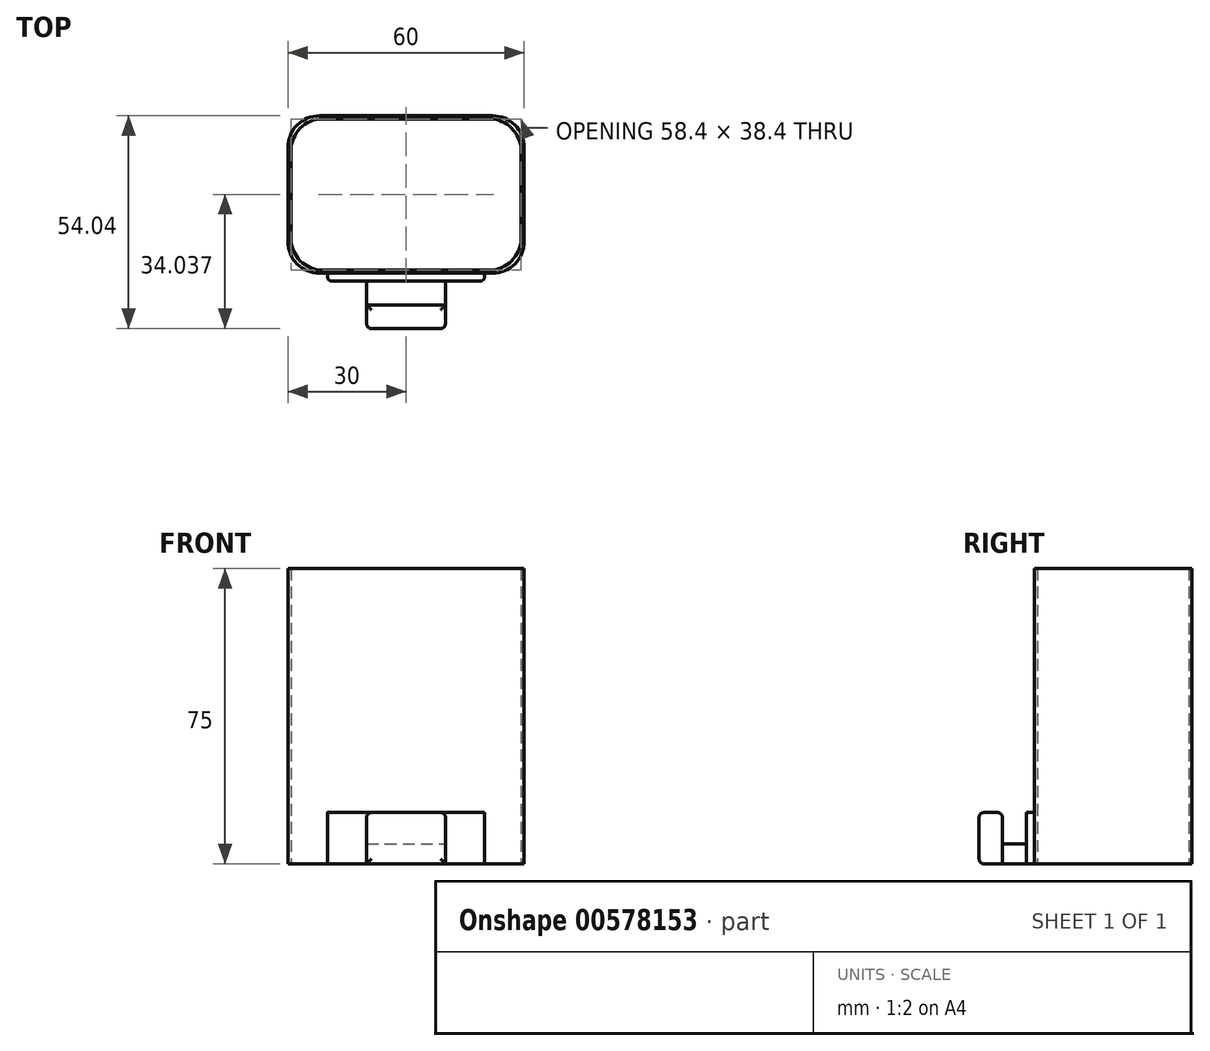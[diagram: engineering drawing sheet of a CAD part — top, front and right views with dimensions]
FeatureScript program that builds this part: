
annotation { "Feature Type Name" : "Feature", "Feature Type Description" : "" }
export const myFeature = defineFeature(function(context is Context, id is Id, definition is map)
    precondition{}
    {
        {
            var Q0;
            Q0=qCreatedBy(makeId("Top.planeOp"),FACE);
            var sketch = newSketch(context, id + "F0", { "sketchPlane" : qUnion([Q0])});
            skLineSegment(sketch, "E0.bottom", {"start": v(30, -33.61) * mm, "end": v(-30, -33.61) * mm});
            skPoint(sketch, "E0.middle", {"position": v(0, 0) * mm});
            skLineSegment(sketch, "E1.bottom", {"start": v(-30, -33.61) * mm, "end": v(30, -33.61) * mm});
            skLineSegment(sketch, "E1.top", {"start": v(-20, -35.61) * mm, "end": v(20, -35.61) * mm});
            skLineSegment(sketch, "E2.top", {"start": v(-10, -41.75) * mm, "end": v(10, -41.75) * mm});
            skLineSegment(sketch, "E3.top", {"start": v(-10, -47.65) * mm, "end": v(10, -47.65) * mm});
            skPoint(sketch, "E4.start.orphan", {"position": v(30, -38.68) * mm});
            skPoint(sketch, "E5.start.orphan", {"position": v(-30, -38.68) * mm});
            skLineSegment(sketch, "E6", {"start": v(-10, -47.65) * mm, "end": v(-10, -35.61) * mm});
            skLineSegment(sketch, "E7", {"start": v(10, -47.65) * mm, "end": v(10, -35.61) * mm});
            skPoint(sketch, "E8.start.orphan", {"position": v(10, -51.4) * mm});
            skPoint(sketch, "E9.start.orphan", {"position": v(-10, -50.9) * mm});
            skPoint(sketch, "E10.orphan", {"position": v(-30, -41.75) * mm});
            skPoint(sketch, "E11.orphan", {"position": v(30, -41.75) * mm});
            skLineSegment(sketch, "E12.top", {"start": v(-30, 6.39) * mm, "end": v(30, 6.39) * mm});
            skLineSegment(sketch, "E12.left", {"start": v(-30, -33.61) * mm, "end": v(-30, 6.39) * mm});
            skLineSegment(sketch, "E12.right", {"start": v(30, -33.61) * mm, "end": v(30, 6.39) * mm});
            skLineSegment(sketch, "E13", {"start": v(20, -35.61) * mm, "end": v(20, -33.61) * mm});
            skLineSegment(sketch, "E14", {"start": v(-20, -35.61) * mm, "end": v(-20, -33.61) * mm});
            skPoint(sketch, "E15.orphan", {"position": v(-30, -35.61) * mm});
            skPoint(sketch, "E16.orphan", {"position": v(30, -35.61) * mm});
            skLineSegment(sketch, "E17.bottom", {"start": v(-29.2, -32.81) * mm, "end": v(29.2, -32.81) * mm});
            skLineSegment(sketch, "E17.top", {"start": v(-29.2, 5.59) * mm, "end": v(29.2, 5.59) * mm});
            skLineSegment(sketch, "E17.left", {"start": v(-29.2, -32.81) * mm, "end": v(-29.2, 5.59) * mm});
            skLineSegment(sketch, "E17.right", {"start": v(29.2, -32.81) * mm, "end": v(29.2, 5.59) * mm});
            skPoint(sketch, "E17.middle", {"position": v(0, -13.61) * mm});
            skSolve(sketch);
        }
        {
            var Q0;
            {var subQ0=sQuery(id+"F0.wireOp",EDGE,"E2.top");Q0=makeQuery(id+"F0.imprint","IMPRINT",FACE,{"disambiguationData":[TD([[makeQuery(id+"F0.imprint","IMPRINT",EDGE,{"derivedFrom":subQ0}),-1.0]])]});}
            var Q1;
            {var subQ0=sQuery(id+"F0.wireOp",EDGE,"E13");Q1=makeQuery(id+"F0.imprint","IMPRINT",FACE,{"disambiguationData":[TD([[makeQuery(id+"F0.imprint","IMPRINT",EDGE,{"derivedFrom":subQ0}),1.0]])]});}
            extrude(context, id + "F1", {"entities" : qUnion([Q0, Q1]), "depth" : 13 * mm, "offsetDistance" : 25 * mm});
        }
        {
            var Q0;
            {var subQ5=sQuery(id+"F0.wireOp",EDGE,"E2.top");Q0=makeQuery(id+"F0.imprint","IMPRINT",FACE,{"disambiguationData":[TD([[makeQuery(id+"F0.imprint","IMPRINT",EDGE,{"derivedFrom":subQ5}),1.0]])]});}
            extrude(context, id + "F2", {"entities" : qUnion([Q0]), "depth" : 5 * mm, "offsetDistance" : 25 * mm});
        }
        {
            var Q0;
            Q0=makeQuery(id+"F0.imprint","IMPRINT",FACE,{"disambiguationData":[TD([[makeQuery(id+"F0.imprint","IMPRINT",EDGE,{"derivedFrom":sQuery(id+"F0.wireOp",EDGE,"E12.top")}),-1.0]])]});
            extrude(context, id + "F3", {"entities" : qUnion([Q0]), "operationType" : NewBodyOperationType.ADD, "depth" : 75 * mm, "offsetDistance" : 25 * mm});
        }
        {
            var Q0;
            Q0=makeQuery(id+"F1.opExtrude","SWEPT_EDGE",EDGE,{"disambiguationData":[OSD([sQuery(id+"F0.wireOp",EDGE,"E3.top"),sQuery(id+"F0.wireOp",EDGE,"E7")])]});
            var Q1;
            Q1=makeQuery(id+"F1.opExtrude","SWEPT_EDGE",EDGE,{"disambiguationData":[OSD([sQuery(id+"F0.wireOp",EDGE,"E3.top"),sQuery(id+"F0.wireOp",EDGE,"E6")])]});
            var Q2;
            Q2=makeQuery(id+"F1.opExtrude","SWEPT_EDGE",EDGE,{"disambiguationData":[OSD([sQuery(id+"F0.wireOp",EDGE,"E1.top"),sQuery(id+"F0.wireOp",EDGE,"E13")])]});
            var Q3;
            Q3=makeQuery(id+"F1.opExtrude","SWEPT_EDGE",EDGE,{"disambiguationData":[OSD([sQuery(id+"F0.wireOp",EDGE,"E1.top"),sQuery(id+"F0.wireOp",EDGE,"E14")])]});
            var Q4;
            Q4=makeQuery(id+"F1.opExtrude","CAP_FACE",FACE,{"disambiguationData":[OSD([sQuery(id+"F0.wireOp",EDGE,"E2.top"),sQuery(id+"F0.wireOp",EDGE,"E3.top"),sQuery(id+"F0.wireOp",EDGE,"E6"),sQuery(id+"F0.wireOp",EDGE,"E7")])],"isStart":false});
            var Q5;
            Q5=makeQuery(id+"F1.opExtrude","CAP_EDGE",EDGE,{"disambiguationData":[OSD([sQuery(id+"F0.wireOp",EDGE,"E3.top")])],"isStart":true});
            fillet(context, id + "F4", {"entities" : qUnion([Q0, Q1, Q2, Q3, Q4, Q5]), "radius" : 1.2 * mm, "tangentPropagation" : true, "allowEdgeOverflow" : false});
        }
        {
            var Q0;
            Q0=makeQuery(id+"F3.opExtrude","SWEPT_EDGE",EDGE,{"disambiguationData":[OSD([sQuery(id+"F0.wireOp",EDGE,"E17.top"),sQuery(id+"F0.wireOp",EDGE,"E17.right")])]});
            var Q1;
            Q1=makeQuery(id+"F3.opExtrude","SWEPT_EDGE",EDGE,{"disambiguationData":[OSD([sQuery(id+"F0.wireOp",EDGE,"E17.bottom"),sQuery(id+"F0.wireOp",EDGE,"E17.right")])]});
            var Q2;
            Q2=makeQuery(id+"F3.opExtrude","SWEPT_EDGE",EDGE,{"disambiguationData":[OSD([sQuery(id+"F0.wireOp",EDGE,"E17.bottom"),sQuery(id+"F0.wireOp",EDGE,"E17.left")])]});
            var Q3;
            Q3=makeQuery(id+"F3.opExtrude","SWEPT_EDGE",EDGE,{"disambiguationData":[OSD([sQuery(id+"F0.wireOp",EDGE,"E17.top"),sQuery(id+"F0.wireOp",EDGE,"E17.left")])]});
            var Q4;
            Q4=makeQuery(id+"F3.opExtrude","SWEPT_EDGE",EDGE,{"disambiguationData":[OSD([sQuery(id+"F0.wireOp",EDGE,"E1.bottom"),sQuery(id+"F0.wireOp",EDGE,"E12.left")])]});
            var Q5;
            Q5=makeQuery(id+"F3.opExtrude","SWEPT_EDGE",EDGE,{"disambiguationData":[OSD([sQuery(id+"F0.wireOp",EDGE,"E12.top"),sQuery(id+"F0.wireOp",EDGE,"E12.left")])]});
            var Q6;
            Q6=makeQuery(id+"F3.opExtrude","SWEPT_EDGE",EDGE,{"disambiguationData":[OSD([sQuery(id+"F0.wireOp",EDGE,"E1.bottom"),sQuery(id+"F0.wireOp",EDGE,"E12.right")])]});
            var Q7;
            Q7=makeQuery(id+"F3.opExtrude","SWEPT_EDGE",EDGE,{"disambiguationData":[OSD([sQuery(id+"F0.wireOp",EDGE,"E12.top"),sQuery(id+"F0.wireOp",EDGE,"E12.right")])]});
            fillet(context, id + "F5", {"entities" : qUnion([Q0, Q1, Q2, Q3, Q4, Q5, Q6, Q7]), "radius" : 8 * mm, "tangentPropagation" : true, "allowEdgeOverflow" : false});
        }
    });
